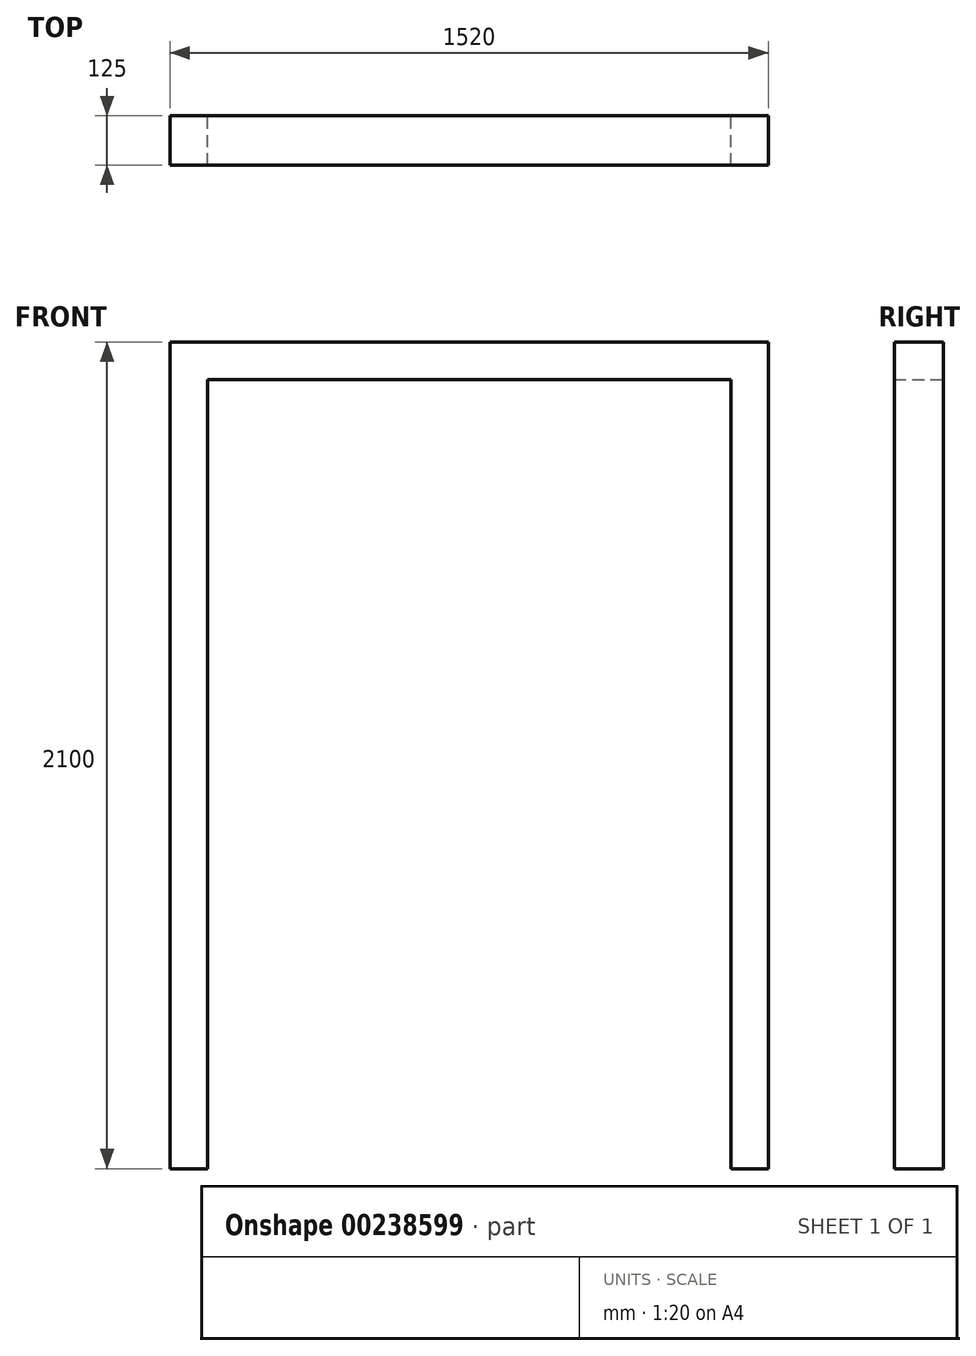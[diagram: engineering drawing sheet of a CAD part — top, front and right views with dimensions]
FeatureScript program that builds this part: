
annotation { "Feature Type Name" : "Feature", "Feature Type Description" : "" }
export const myFeature = defineFeature(function(context is Context, id is Id, definition is map)
    precondition{}
    {
        {
            var Q0;
            Q0=qCreatedBy(makeId("Front.planeOp"),FACE);
            var sketch = newSketch(context, id + "F0", { "sketchPlane" : qUnion([Q0])});
            skLineSegment(sketch, "E0.bottom", {"start": v(-760, 1050) * mm, "end": v(760, 1050) * mm});
            skLineSegment(sketch, "E0.top", {"start": v(-760, -1050) * mm, "end": v(-665, -1050) * mm});
            skLineSegment(sketch, "E0.left", {"start": v(-760, 1050) * mm, "end": v(-760, -1050) * mm});
            skLineSegment(sketch, "E0.right", {"start": v(760, 1050) * mm, "end": v(760, -1050) * mm});
            skPoint(sketch, "E0.middle", {"position": v(0, 0) * mm});
            skLineSegment(sketch, "E1", {"start": v(-665, -1050) * mm, "end": v(-665, 955) * mm});
            skLineSegment(sketch, "E2", {"start": v(-665, 955) * mm, "end": v(665, 955) * mm});
            skLineSegment(sketch, "E3", {"start": v(665, 955) * mm, "end": v(665, -1050) * mm});
            skLineSegment(sketch, "E4.trimOffspring", {"start": v(665, -1050) * mm, "end": v(760, -1050) * mm});
            skSolve(sketch);
        }
        {
            var Q0;
            Q0=makeQuery(id+"F0.imprint","IMPRINT",FACE,{"disambiguationData":[TD([[makeQuery(id+"F0.imprint","IMPRINT",EDGE,{"derivedFrom":sQuery(id+"F0.wireOp",EDGE,"E0.bottom")}),-1.0]])]});
            extrude(context, id + "F1", {"entities" : qUnion([Q0]), "depth" : 125 * mm});
        }
    });
